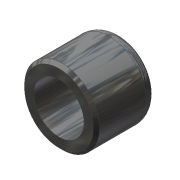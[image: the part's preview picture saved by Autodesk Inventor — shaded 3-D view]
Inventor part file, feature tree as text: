
AUTODESK INVENTOR PART (.ipt)
format: ipt  version: unknown  size: 182,784 bytes
history: native  units: mm (DEFAULTED — no unit token found)
features: extrude x1, fillet x1, chamfer x1, sketch x1
ambient origin geometry x8: Origin, YZ Plane, XZ Plane, XY Plane, X Axis, Y Axis, Z Axis, Center Point
feature tree (4):
  extrude  "Extrusion1"  Depth=12.7mm
  fillet  "Fillet1"  Radius=15.875mm
  chamfer  "Chamfer1"  Distance=3.175mm
  sketch  "Sketch1"  dims[d0=19.05mm d1=12.7mm d2=15.875mm d3=0.0mm d4=3.175mm d5=0.7874mm d6=3.175mm d7=45.0deg]
